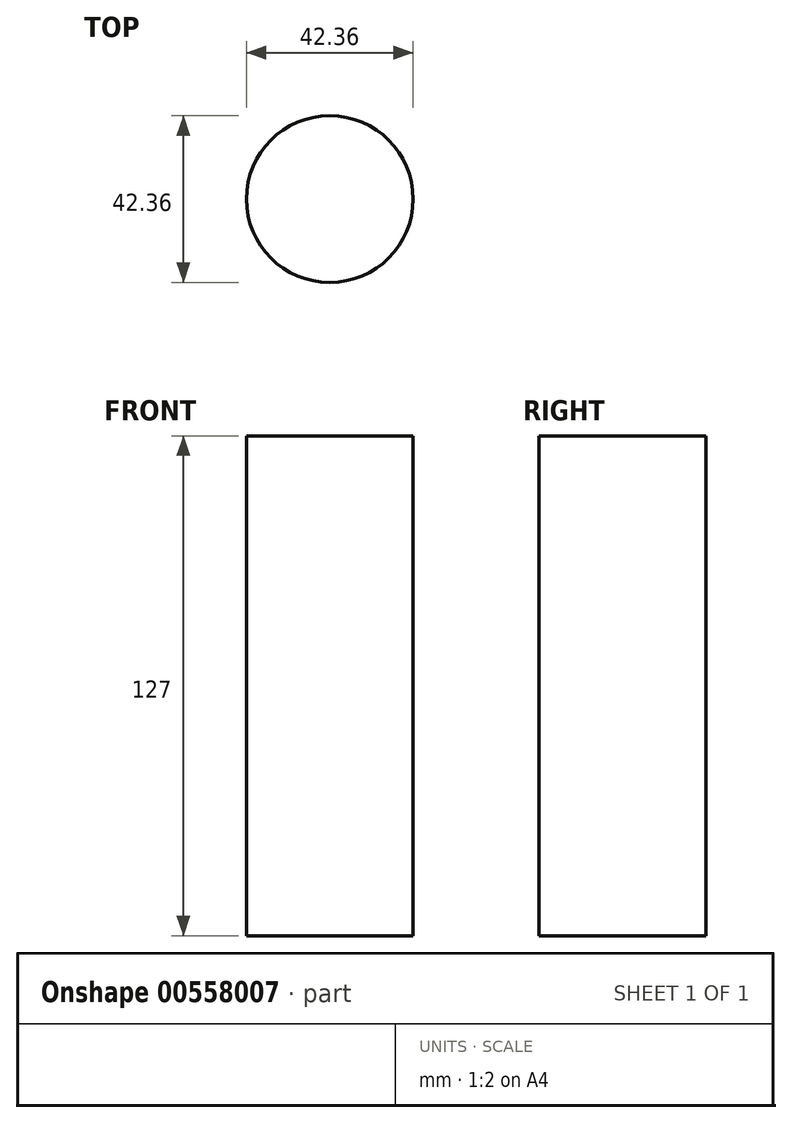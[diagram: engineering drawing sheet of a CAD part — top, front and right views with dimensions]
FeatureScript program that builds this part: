
annotation { "Feature Type Name" : "Feature", "Feature Type Description" : "" }
export const myFeature = defineFeature(function(context is Context, id is Id, definition is map)
    precondition{}
    {
        {
            var Q0;
            Q0=qCreatedBy(makeId("Top.planeOp"),FACE);
            var sketch = newSketch(context, id + "F0", { "sketchPlane" : qUnion([Q0])});
            skCircle(sketch, "E0", {"center": v(0, 0) * mm, "radius": 21.18 * mm});
            skSolve(sketch);
        }
        {
            var Q0;
            Q0=sQuery(id+"F0.wireOp",EDGE,"E0");
            extrude(context, id + "F1", {"bodyType" : ToolBodyType.SURFACE, "surfaceEntities" : qUnion([Q0]), "depth" : 127 * mm, "offsetDistance" : 25.4 * mm});
        }
    });
